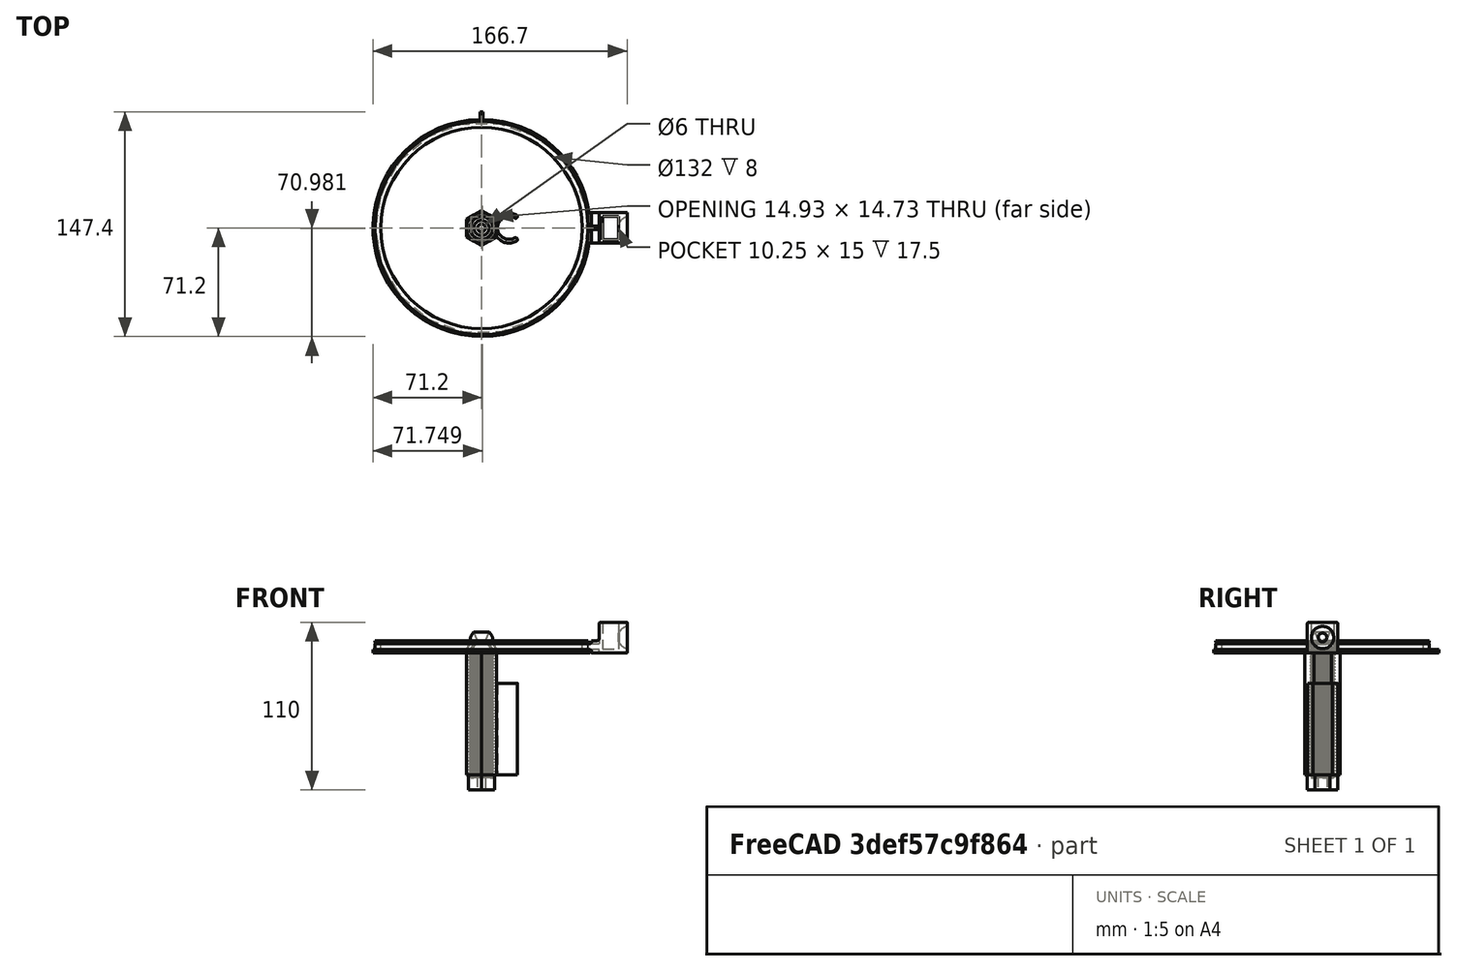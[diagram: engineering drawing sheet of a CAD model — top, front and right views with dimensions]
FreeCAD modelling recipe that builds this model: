
FCSTD DOCUMENT  (FreeCAD 0.17R13519 (Git))
Label: Pop Filter
License: All rights reserved
LicenseURL: http://en.wikipedia.org/wiki/All_rights_reserved
objects: Sketcher::SketchObject×17, PartDesign::Pad×8, PartDesign::Body×5, App::Part×5, PartDesign::Pocket×5, PartDesign::Revolution×4, PartDesign::Plane×2, PartDesign::Fillet×2, Part::FeaturePython×2, PartDesign::Line×1, PartDesign::Groove×1, PartDesign::Chamfer×1, PartDesign::Boolean×1, PartDesign::FeatureBase×1
note: 68 computed .brp shape members not serialized (recipe doc carries the construction recipe); baked Part::Feature solids carry a one-line shape summary decoded from their .brp

FEATURE [Sketcher::SketchObject] Sketch001  label="Sketch"
  MapMode = 5
  Placement = pos=(0,0,0) rot=(1,0,0;1.5708rad)
  Support = -> [XZ_Plane]
  sketch-geometry (6):
    g0: ArcOfCircle CenterX=0 CenterY=8 CenterZ=0 NormalX=0 NormalY=0 NormalZ=1 AngleXU=0 Radius=7.5 StartAngle=6.03051 EndAngle=7.12425
    g1: ArcOfCircle CenterX=0 CenterY=0 CenterZ=0 NormalX=0 NormalY=0 NormalZ=1 AngleXU=0 Radius=7.5 StartAngle=0 EndAngle=0.841069
    g2: ArcOfCircle CenterX=0 CenterY=0 CenterZ=0 NormalX=0 NormalY=0 NormalZ=1 AngleXU=0 Radius=9.5 StartAngle=0 EndAngle=0.700679
    g3: LineSegment StartX=5 StartY=5.59017 StartZ=0 EndX=2.5 EndY=8 EndZ=0
    g4: LineSegment StartX=7.5 StartY=0 StartZ=0 EndX=9.5 EndY=0 EndZ=0
    g5: LineSegment StartX=2.5 StartY=8 StartZ=0 EndX=5 EndY=13.5902 EndZ=0
  constraints (19):
    c: PointOnObject(g0,g-2)
    c: Radius(g0) = 7.5
    c: Coincident(g1,g-1)
    c: DistanceY(g-1,g1) = 0
    c: DistanceX(g-1,g1) = 5
    c: Radius(g1) = 7.5
    c: Coincident(g2,g-1)
    c: Coincident(g2,g0)
    c: PointOnObject(g2,g-1)
    c: DistanceX(g1,g2) = 2
    c: Coincident(g3,g1)
    c: Coincident(g4,g1)
    c: Coincident(g4,g2)
    c: DistanceY(g0,g3) = 0
    c: DistanceX(g0,g3) = 2.5
    c: Coincident(g5,g3)
    c: Coincident(g5,g0)
    c: DistanceX(g0,g0) = 5
    c: DistanceY(g-1,g0) = 8
FEATURE [PartDesign::Revolution] Revolution
  Angle = 360
  Axis = (0,0,1)
  Base = (0,0,0)
  Placement = pos=(0,0,0) rot=(1,0,0;1.5708rad)
  Profile = -> Sketch001
  ReferenceAxis = -> Sketch001 [V_Axis]
  Reversed = true
FEATURE [PartDesign::Body] Body  label="Arm Section Body"
  Group = -> [Sketch001,Revolution]
  Origin = -> Origin
  Tip = -> Revolution
FEATURE [App::Part] Part  label="Arm Section"
  Group = -> [Body]
  License = CC BY 3.0
  LicenseURL = http://creativecommons.org/licenses/by/3.0/
  Origin = -> Origin001
FEATURE [Sketcher::SketchObject] Sketch002  label="Sketch001"
  MapMode = 5
  Placement = pos=(0,0,0) rot=(1,0,0;1.5708rad)
  Support = -> [XZ_Plane002]
  sketch-geometry (8):
    g0: LineSegment StartX=70 StartY=1 StartZ=0 EndX=70 EndY=0 EndZ=0
    g1: ArcOfCircle CenterX=70 CenterY=1.5 CenterZ=0 NormalX=0 NormalY=0 NormalZ=1 AngleXU=0 Radius=0.5 StartAngle=1.5708 EndAngle=4.71239
    g2: LineSegment StartX=70 StartY=8 StartZ=0 EndX=70 EndY=7 EndZ=0
    g3: ArcOfCircle CenterX=70 CenterY=6.5 CenterZ=0 NormalX=0 NormalY=0 NormalZ=1 AngleXU=0 Radius=0.5 StartAngle=1.5708 EndAngle=4.71239
    g4: LineSegment StartX=70 StartY=2 StartZ=0 EndX=70 EndY=6 EndZ=0
    g5: LineSegment StartX=70 StartY=0 StartZ=0 EndX=66 EndY=0 EndZ=0
    g6: LineSegment StartX=66 StartY=0 StartZ=0 EndX=66 EndY=8 EndZ=0
    g7: LineSegment StartX=66 StartY=8 StartZ=0 EndX=70 EndY=8 EndZ=0
  constraints (27):
    c: Vertical(g0)
    c: PointOnObject(g0,g-1)
    c: DistanceX(g-1,g0) = 70  '70'
    c: Coincident(g1,g0)
    c: DistanceX(g0,g1) = 0
    c: DistanceY(g0,g0) = 1
    c: Radius(g1) = 0.5
    c: Vertical(g2)
    c: DistanceY(g2,g2) = 1
    c: Coincident(g3,g2)
    c: Radius(g3) = 0.5
    c: DistanceX(g2,g3) = 0
    c: Coincident(g4,g1)
    c: Coincident(g4,g3)
    c: Vertical(g4)
    c: DistanceX(g3,g2) = 0
    c: DistanceX(g1,g0) = 0
    c: DistanceY(g0,g2) = 8
    c: Coincident(g6,g5)
    c: Vertical(g6)
    c: PointOnObject(g7,g6)
    c: Horizontal(g7)
    c: Horizontal(g5)
    c: Coincident(g6,g7)
    c: Coincident(g0,g5)
    c: Coincident(g7,g2)
    c: DistanceX(g7,g7) = 4
FEATURE [PartDesign::Revolution] Revolution001
  Angle = 360
  Axis = (0,0,1)
  Base = (0,0,0)
  Placement = pos=(0,0,0) rot=(1,0,0;1.5708rad)
  Profile = -> Sketch002
  ReferenceAxis = -> Sketch002 [V_Axis]
  Reversed = true
FEATURE [PartDesign::Plane] DatumPlane
  MapMode = 49
  Placement = pos=(70,-1e-12,6) rot=(0,1,0;1.5708rad)
  Support = -> [Revolution001]
FEATURE [Sketcher::SketchObject] Sketch  label="Sketch002"
  ExternalGeometry = -> [Revolution001]
  MapMode = 5
  Placement = pos=(70,-1e-12,6) rot=(0,1,0;1.5708rad)
  Support = -> [DatumPlane]
  sketch-geometry (4):
    g0: LineSegment StartX=0 StartY=10 StartZ=0 EndX=4 EndY=10 EndZ=0
    g1: LineSegment StartX=4 StartY=10 StartZ=0 EndX=4 EndY=-10 EndZ=0
    g2: LineSegment StartX=4 StartY=-10 StartZ=0 EndX=0 EndY=-10 EndZ=0
    g3: LineSegment StartX=0 StartY=-10 StartZ=0 EndX=0 EndY=10 EndZ=0
  constraints (11):
    c: Coincident(g1,g2)
    c: Coincident(g2,g3)
    c: Coincident(g3,g0)
    c: Horizontal(g0)
    c: Horizontal(g2)
    c: Vertical(g1)
    c: Vertical(g3)
    c: DistanceY(g1,g1) = 20  '7.5*2+2.5*2'
    c: Coincident(g1,g0)
    c: Symmetric(g0,g1,g-3)
    c: Symmetric(g0,g2,g-1)
FEATURE [PartDesign::Pad] Pad
  BaseFeature = -> Revolution001
  Length = 2
  Length2 = 2
  Placement = pos=(0,0,0) rot=(1,0,0;1.5708rad)
  Profile = -> Sketch
  Type = 4
FEATURE [Sketcher::SketchObject] Sketch003
  ExternalGeometry = -> [Pad]
  MapMode = 5
  Placement = pos=(72,0,0) rot=(0.707107,0,0.707107;3.14159rad)
  Support = -> [Pad]
  sketch-geometry (4):
    g0: LineSegment StartX=0 StartY=10 StartZ=0 EndX=8 EndY=10 EndZ=0
    g1: LineSegment StartX=8 StartY=10 StartZ=0 EndX=8 EndY=-10 EndZ=0
    g2: LineSegment StartX=8 StartY=-10 StartZ=0 EndX=0 EndY=-10 EndZ=0
    g3: LineSegment StartX=0 StartY=-10 StartZ=0 EndX=0 EndY=10 EndZ=0
  constraints (12):
    c: Coincident(g0,g1)
    c: Coincident(g1,g2)
    c: Coincident(g2,g3)
    c: Coincident(g3,g0)
    c: Horizontal(g0)
    c: Horizontal(g2)
    c: Vertical(g1)
    c: Vertical(g3)
    c: PointOnObject(g-6,g0)
    c: PointOnObject(g-4,g2)
    c: PointOnObject(g-1,g3)
    c: PointOnObject(g-7,g1)
FEATURE [PartDesign::Pad] Pad001
  BaseFeature = -> Pad
  Length = 5
  Length2 = 100
  Placement = pos=(0,0,0) rot=(1,0,0;1.5708rad)
  Profile = -> Sketch003
  Type = 0
FEATURE [Sketcher::SketchObject] Sketch004
  ExternalGeometry = -> [Pad001]
  MapMode = 5
  Placement = pos=(0,0,0) rot=(1,0,0;3.14159rad)
  Support = -> [Pad001]
  sketch-geometry (4):
    g0: LineSegment StartX=72 StartY=1.1 StartZ=0 EndX=77 EndY=1.1 EndZ=0
    g1: LineSegment StartX=77 StartY=1.1 StartZ=0 EndX=77 EndY=-1.1 EndZ=0
    g2: LineSegment StartX=77 StartY=-1.1 StartZ=0 EndX=72 EndY=-1.1 EndZ=0
    g3: LineSegment StartX=72 StartY=-1.1 StartZ=0 EndX=72 EndY=1.1 EndZ=0
  constraints (12):
    c: Coincident(g0,g1)
    c: Coincident(g1,g2)
    c: Coincident(g2,g3)
    c: Coincident(g3,g0)
    c: Horizontal(g0)
    c: Horizontal(g2)
    c: Vertical(g1)
    c: Vertical(g3)
    c: PointOnObject(g0,g-3)
    c: PointOnObject(g0,g-4)
    c: Symmetric(g0,g2,g-1)
    c: DistanceY(g1,g0) = 2.2
FEATURE [PartDesign::Pocket] Pocket
  BaseFeature = -> Pad001
  Length = 2
  Length2 = 100
  Placement = pos=(0,0,0) rot=(1,0,0;1.5708rad)
  Profile = -> Sketch004
  Type = 0
FEATURE [Sketcher::SketchObject] Sketch005
  ExternalGeometry = -> [Pocket]
  MapMode = 5
  Placement = pos=(0,-1e-12,8) rot=(0,0,1;3.14159rad)
  Support = -> [Pocket]
  sketch-geometry (4):
    g0: LineSegment StartX=-77 StartY=1.1 StartZ=0 EndX=-72 EndY=1.1 EndZ=0
    g1: LineSegment StartX=-72 StartY=1.1 StartZ=0 EndX=-72 EndY=-1.1 EndZ=0
    g2: LineSegment StartX=-72 StartY=-1.1 StartZ=0 EndX=-77 EndY=-1.1 EndZ=0
    g3: LineSegment StartX=-77 StartY=-1.1 StartZ=0 EndX=-77 EndY=1.1 EndZ=0
  constraints (12):
    c: Coincident(g0,g1)
    c: Coincident(g1,g2)
    c: Coincident(g2,g3)
    c: Coincident(g3,g0)
    c: Horizontal(g0)
    c: Horizontal(g2)
    c: Vertical(g1)
    c: Vertical(g3)
    c: PointOnObject(g0,g-3)
    c: Symmetric(g0,g1,g-1)
    c: DistanceY(g2,g0) = 2.2
    c: PointOnObject(g0,g-4)
FEATURE [PartDesign::Pocket] Pocket001
  BaseFeature = -> Pocket
  Length = 2
  Length2 = 100
  Placement = pos=(0,0,0) rot=(1,0,0;1.5708rad)
  Profile = -> Sketch005
  Type = 0
FEATURE [Sketcher::SketchObject] Sketch006
  ExternalGeometry = -> [Pocket001]
  MapMode = 5
  Placement = pos=(77,0,0) rot=(0.707107,0,0.707107;3.14159rad)
  Support = -> [Pocket001]
  sketch-geometry (4):
    g0: LineSegment StartX=0 StartY=10 StartZ=0 EndX=20 EndY=10 EndZ=0
    g1: LineSegment StartX=20 StartY=10 StartZ=0 EndX=20 EndY=-10 EndZ=0
    g2: LineSegment StartX=20 StartY=-10 StartZ=0 EndX=0 EndY=-10 EndZ=0
    g3: LineSegment StartX=0 StartY=-10 StartZ=0 EndX=0 EndY=10 EndZ=0
  constraints (12):
    c: Coincident(g0,g1)
    c: Coincident(g1,g2)
    c: Coincident(g2,g3)
    c: Coincident(g3,g0)
    c: Horizontal(g0)
    c: Horizontal(g2)
    c: Vertical(g1)
    c: Vertical(g3)
    c: PointOnObject(g-3,g0)
    c: Symmetric(g0,g1,g-1)
    c: PointOnObject(g-1,g3)
    c: DistanceX(g0,g0) = 20  '7.5*2+2.5*2'
FEATURE [PartDesign::Pad] Pad002
  BaseFeature = -> Pocket001
  Length = 18.5
  Length2 = 100
  Placement = pos=(0,0,0) rot=(1,0,0;1.5708rad)
  Profile = -> Sketch006
  Type = 0
FEATURE [Sketcher::SketchObject] Sketch007
  AttachmentOffset = pos=(0,0,1.5) rot=(0,0,1;0rad)
  ExternalGeometry = -> [Pad002]
  MapMode = 5
  Placement = pos=(97,0,0) rot=(0.707107,0,0.707107;3.14159rad)
  Support = -> [Pad002]
  sketch-geometry (2):
    g0: ArcOfCircle CenterX=10 CenterY=0 CenterZ=0 NormalX=0 NormalY=0 NormalZ=1 AngleXU=0 Radius=7.5 StartAngle=3.14159 EndAngle=6.28319
    g1: LineSegment StartX=17.5 StartY=0 StartZ=0 EndX=2.5 EndY=0 EndZ=0
  constraints (7):
    c: PointOnObject(g0,g-1)
    c: PointOnObject(g0,g-1)
    c: PointOnObject(g0,g-1)
    c: Radius(g0) = 7.5
    c: DistanceX(g0,g-3) = 2.5
    c: Coincident(g1,g0)
    c: Coincident(g1,g0)
FEATURE [PartDesign::Line] DatumLine
  AttacherType = Attacher::AttachEngineLine
  MapMode = 29
  Placement = pos=(97,0,0) rot=(0,1,0;3.14159rad)
  Support = -> [Sketch007]
FEATURE [PartDesign::Groove] Groove
  Angle = 360
  Axis = (0,0,-1)
  Base = (97,0,0)
  BaseFeature = -> Pad002
  Placement = pos=(0,0,0) rot=(1,0,0;1.5708rad)
  Profile = -> Sketch007
  ReferenceAxis = -> DatumLine
FEATURE [Sketcher::SketchObject] Sketch008
  ExternalGeometry = -> [Groove]
  MapMode = 5
  Placement = pos=(0,-2e-12,20) rot=(0,0,1;3.14159rad)
  Support = -> [Groove]
  sketch-geometry (4):
    g0: LineSegment StartX=-89.75 StartY=7.5 StartZ=0 EndX=-79.5 EndY=7.5 EndZ=0
    g1: LineSegment StartX=-79.5 StartY=7.5 StartZ=0 EndX=-79.5 EndY=-7.5 EndZ=0
    g2: LineSegment StartX=-79.5 StartY=-7.5 StartZ=0 EndX=-89.75 EndY=-7.5 EndZ=0
    g3: LineSegment StartX=-89.75 StartY=-7.5 StartZ=0 EndX=-89.75 EndY=7.5 EndZ=0
  constraints (12):
    c: Coincident(g0,g1)
    c: Coincident(g1,g2)
    c: Coincident(g2,g3)
    c: Coincident(g3,g0)
    c: Horizontal(g0)
    c: Horizontal(g2)
    c: Vertical(g1)
    c: Vertical(g3)
    c: DistanceY(g-3,g2) = 2.5
    c: DistanceY(g0,g-3) = 2.5
    c: DistanceX(g-3,g0) = 5.75
    c: DistanceX(g0,g-4) = 2.5
FEATURE [PartDesign::Pocket] Pocket002
  BaseFeature = -> Groove
  Length = 17.5
  Length2 = 100
  Placement = pos=(0,0,0) rot=(1,0,0;1.5708rad)
  Profile = -> Sketch008
  Type = 0
FEATURE [PartDesign::Fillet] Fillet
  Base = -> Pocket002 [Edge37,Edge38,Edge64,Edge75,Edge13,Edge10]
  BaseFeature = -> Pocket002
  Placement = pos=(0,0,0) rot=(1,0,0;1.5708rad)
  Radius = 1
FEATURE [PartDesign::Chamfer] Chamfer
  Base = -> Fillet [Edge118]
  BaseFeature = -> Fillet
  Placement = pos=(0,0,0) rot=(1,0,0;1.5708rad)
  Size = 1
FEATURE [PartDesign::Fillet] Fillet001
  Base = -> Chamfer [Face25,Face34,Edge18,Edge36,Edge24,Edge15,Edge16,Edge41,Edge50]
  BaseFeature = -> Chamfer
  Placement = pos=(0,0,0) rot=(1,0,0;1.5708rad)
  Radius = 1
FEATURE [PartDesign::Body] Body001  label="Pop Filter Body"
  Group = -> [Sketch002,Revolution001,DatumPlane,Sketch,Pad,Sketch003,Pad001,Sketch004,Pocket,Sketch005,Pocket001,Sketch006,Pad002,Sketch007,DatumLine,Groove,Sketch008,Pocket002,Fillet,Chamfer,Fillet001]
  Origin = -> Origin002
  Tip = -> Fillet001
FEATURE [App::Part] Part001  label="Pop Filter"
  Group = -> [Body001]
  License = CC BY 3.0
  LicenseURL = http://creativecommons.org/licenses/by/3.0/
  Origin = -> Origin003
FEATURE [Sketcher::SketchObject] Sketch009
  MapMode = 5
  Placement = pos=(0,0,0) rot=(0.57735,0.57735,0.57735;2.0944rad)
  Support = -> [YZ_Plane004]
  sketch-geometry (5):
    g0: LineSegment StartX=70.2 StartY=1 StartZ=0 EndX=70.2 EndY=0 EndZ=0
    g1: ArcOfCircle CenterX=70.2 CenterY=1.5 CenterZ=0 NormalX=0 NormalY=0 NormalZ=1 AngleXU=0 Radius=0.5 StartAngle=1.5708 EndAngle=4.71239
    g2: LineSegment StartX=70.2 StartY=0 StartZ=0 EndX=71.2 EndY=0 EndZ=0
    g3: LineSegment StartX=70.2 StartY=2 StartZ=0 EndX=71.2 EndY=2 EndZ=0
    g4: LineSegment StartX=71.2 StartY=2 StartZ=0 EndX=71.2 EndY=0 EndZ=0
  constraints (16):
    c: Vertical(g0)
    c: PointOnObject(g0,g-1)
    c: DistanceX(g-1,g0) = 70.2  '70.2'
    c: Coincident(g1,g0)
    c: DistanceX(g0,g1) = 0
    c: DistanceY(g0,g0) = 1
    c: Radius(g1) = 0.5
    c: DistanceX(g1,g0) = 0
    c: Coincident(g2,g0)
    c: PointOnObject(g2,g-1)
    c: Coincident(g3,g1)
    c: Horizontal(g3)
    c: Coincident(g4,g3)
    c: Coincident(g4,g2)
    c: Vertical(g4)
    c: DistanceX(g2,g2) = 1
FEATURE [PartDesign::Revolution] Revolution002
  Angle = 360
  Axis = (0,0,1)
  Base = (0,0,0)
  Placement = pos=(0,0,0) rot=(0.57735,0.57735,0.57735;2.0944rad)
  Profile = -> Sketch009
  ReferenceAxis = -> Sketch009 [V_Axis]
  Reversed = true
FEATURE [PartDesign::Plane] DatumPlane001
  MapMode = 52
  Placement = pos=(0,71.2,2) rot=(-1,0,0;1.5708rad)
  Support = -> [Revolution002]
FEATURE [Sketcher::SketchObject] Sketch010
  ExternalGeometry = -> [Revolution002]
  MapMode = 5
  Placement = pos=(0,71.2,2) rot=(-1,0,0;1.5708rad)
  Support = -> [DatumPlane001]
  sketch-geometry (4):
    g0: LineSegment StartX=-1.1 StartY=2 StartZ=0 EndX=1.1 EndY=2 EndZ=0
    g1: LineSegment StartX=1.1 StartY=2 StartZ=0 EndX=1.1 EndY=0 EndZ=0
    g2: LineSegment StartX=1.1 StartY=0 StartZ=0 EndX=-1.1 EndY=0 EndZ=0
    g3: LineSegment StartX=-1.1 StartY=0 StartZ=0 EndX=-1.1 EndY=2 EndZ=0
  constraints (11):
    c: Coincident(g0,g1)
    c: Coincident(g1,g2)
    c: Coincident(g2,g3)
    c: Coincident(g3,g0)
    c: Horizontal(g0)
    c: Horizontal(g2)
    c: Vertical(g1)
    c: Vertical(g3)
    c: Symmetric(g1,g2,g-1)
    c: PointOnObject(g-3,g0)
    c: DistanceX(g0,g0) = 2.2
FEATURE [PartDesign::Pad] Pad003
  BaseFeature = -> Revolution002
  Length = 5
  Length2 = 1
  Placement = pos=(0,0,0) rot=(0.57735,0.57735,0.57735;2.0944rad)
  Profile = -> Sketch010
  Type = 4
FEATURE [Sketcher::SketchObject] Sketch011
  ExternalGeometry = -> [Pad003]
  MapMode = 5
  Placement = pos=(0,0,2) rot=(0,0,-1;1.5708rad)
  Support = -> [Pad003]
  sketch-geometry (4):
    g0: LineSegment StartX=-76.2 StartY=0.1 StartZ=0 EndX=0 EndY=0.1 EndZ=0
    g1: LineSegment StartX=0 StartY=0.1 StartZ=0 EndX=0 EndY=-0.1 EndZ=0
    g2: LineSegment StartX=0 StartY=-0.1 StartZ=0 EndX=-76.2 EndY=-0.1 EndZ=0
    g3: LineSegment StartX=-76.2 StartY=-0.1 StartZ=0 EndX=-76.2 EndY=0.1 EndZ=0
  constraints (12):
    c: Coincident(g0,g1)
    c: Coincident(g1,g2)
    c: Coincident(g2,g3)
    c: Coincident(g3,g0)
    c: Horizontal(g0)
    c: Horizontal(g2)
    c: Vertical(g1)
    c: Vertical(g3)
    c: Symmetric(g1,g0,g-1)
    c: DistanceY(g1,g0) = 0.2
    c: PointOnObject(g2,g-3)
    c: PointOnObject(g1,g-2)
FEATURE [PartDesign::Pocket] Pocket003
  BaseFeature = -> Pad003
  Length = 2
  Length2 = 100
  Placement = pos=(0,0,0) rot=(0.57735,0.57735,0.57735;2.0944rad)
  Profile = -> Sketch011
  Type = 0
FEATURE [Sketcher::SketchObject] Sketch012
  MapMode = 5
  Placement = pos=(0,0,0) rot=(1,0,0;1.5708rad)
  Support = -> [XZ_Plane006]
  sketch-geometry (5):
    g0: ArcOfCircle CenterX=0 CenterY=8 CenterZ=0 NormalX=0 NormalY=0 NormalZ=1 AngleXU=0 Radius=7.5 StartAngle=6.11362 EndAngle=7.12425
    g1: ArcOfCircle CenterX=0 CenterY=0 CenterZ=0 NormalX=0 NormalY=0 NormalZ=1 AngleXU=0 Radius=10 StartAngle=0 EndAngle=0.738849
    g2: LineSegment StartX=8 StartY=0 StartZ=0 EndX=10 EndY=0 EndZ=0
    g3: LineSegment StartX=2.5 StartY=8 StartZ=0 EndX=5 EndY=13.5902 EndZ=0
    g4: LineSegment StartX=2.5 StartY=8 StartZ=0 EndX=8 EndY=0 EndZ=0
  constraints (16):
    c: PointOnObject(g0,g-2)
    c: Radius(g0) = 7.5
    c: DistanceY(g-1,g2) = 0
    c: Coincident(g1,g-1)
    c: Coincident(g1,g0)
    c: PointOnObject(g1,g-1)
    c: Coincident(g2,g1)
    c: DistanceY(g0,g3) = 0
    c: DistanceX(g0,g3) = 2.5
    c: Coincident(g3,g0)
    c: DistanceX(g0,g0) = 5
    c: DistanceY(g-1,g0) = 8
    c: DistanceX(g-1,g1) = 10
    c: Coincident(g4,g2)
    c: Coincident(g4,g3)
    c: DistanceX(g-1,g2) = 8
FEATURE [PartDesign::Revolution] Revolution003
  Angle = 360
  Axis = (0,0,1)
  Base = (0,0,0)
  Placement = pos=(0,0,0) rot=(1,0,0;1.5708rad)
  Profile = -> Sketch012
  ReferenceAxis = -> Sketch012 [V_Axis]
  Reversed = true
FEATURE [PartDesign::Pad] Pad004
  BaseFeature = -> Pocket003
  Length = 10
  Length2 = 100
  Placement = pos=(0,0,0) rot=(0.57735,0.57735,0.57735;2.0944rad)
  Profile = -> Revolution003 [Face4]
  Type = 0
FEATURE [PartDesign::Body] Body002  label="Pop Filter Ring Body"
  Group = -> [Sketch009,Revolution002,DatumPlane001,Sketch010,Pad003,Sketch011,Pocket003,Pad004]
  Origin = -> Origin005
  Tip = -> Pad004
FEATURE [App::Part] Part002  label="Pop Filter Ring"
  Group = -> [Body002]
  License = CC BY 3.0
  LicenseURL = http://creativecommons.org/licenses/by/3.0/
  Origin = -> Origin004
FEATURE [Sketcher::SketchObject] Sketch013
  ExternalGeometry = -> [Revolution003]
  MapMode = 5
  Placement = pos=(0,0,0) rot=(1,0,0;3.14159rad)
  Support = -> [Revolution003]
  sketch-geometry (7):
    g0: LineSegment StartX=10 StartY=-5.7735 StartZ=0 EndX=10 EndY=5.7735 EndZ=0
    g1: LineSegment StartX=10 StartY=5.7735 StartZ=0 EndX=0 EndY=11.547 EndZ=0
    g2: LineSegment StartX=0 StartY=11.547 StartZ=0 EndX=-10 EndY=5.7735 EndZ=0
    g3: LineSegment StartX=-10 StartY=5.7735 StartZ=0 EndX=-10 EndY=-5.7735 EndZ=0
    g4: LineSegment StartX=-10 StartY=-5.7735 StartZ=0 EndX=0 EndY=-11.547 EndZ=0
    g5: LineSegment StartX=0 StartY=-11.547 StartZ=0 EndX=10 EndY=-5.7735 EndZ=0
    g6: Circle [constr] CenterX=0 CenterY=0 CenterZ=0 NormalX=0 NormalY=0 NormalZ=1 AngleXU=0 Radius=11.547
  constraints (16):
    c: Coincident(g0,g1)
    c: Coincident(g1,g2)
    c: Coincident(g2,g3)
    c: Coincident(g3,g4)
    c: Coincident(g4,g5)
    c: Coincident(g5,g0)
    c: Equal(g0, g1-g5) x5
    c: PointOnObject(g0,g6)
    c: PointOnObject(g1,g6)
    c: PointOnObject(g2,g6)
    c: PointOnObject(g3,g6)
    c: PointOnObject(g4,g6)
    c: PointOnObject(g5,g6)
    c: Vertical(g0)
    c: Coincident(g6,g-1)
    c: Tangent(g-3,g0)
FEATURE [PartDesign::Pad] Pad005
  BaseFeature = -> Revolution003
  Length = 80
  Length2 = 100
  Placement = pos=(0,0,0) rot=(1,0,0;1.5708rad)
  Profile = -> Sketch013
  Type = 0
FEATURE [Part::FeaturePython] ScrewTap  label="M16x80.0-ScrewTap"  # Fasteners workbench fastener (typed FeaturePython)
  diameter = 13
  invert = false
  length = 80
  matchOuter = false
  offset = 0
  thread = true
FEATURE [PartDesign::Boolean] Boolean
  BaseFeature = -> Pad005
  Group = -> [ScrewTap]
  Type = 1
FEATURE [Sketcher::SketchObject] Sketch014
  ExternalGeometry = -> [Boolean]
  MapMode = 5
  Placement = pos=(0,8e-12,-80) rot=(1,0,0;3.14159rad)
  Support = -> [Boolean]
  sketch-geometry (8):
    g0: ArcOfCircle CenterX=18 CenterY=0 CenterZ=0 NormalX=0 NormalY=0 NormalZ=1 AngleXU=0 Radius=7.5 StartAngle=1.0472 EndAngle=5.23599
    g1: ArcOfCircle CenterX=18 CenterY=0 CenterZ=0 NormalX=0 NormalY=0 NormalZ=1 AngleXU=0 Radius=9.86577 StartAngle=3.76673 EndAngle=5.23599
    g2: ArcOfCircle CenterX=22.3414 CenterY=-7.5196 CenterZ=0 NormalX=0 NormalY=0 NormalZ=1 AngleXU=0 Radius=1.18288 StartAngle=5.23599 EndAngle=8.37758
    g3: ArcOfCircle CenterX=22.3414 CenterY=7.5196 CenterZ=0 NormalX=0 NormalY=0 NormalZ=1 AngleXU=0 Radius=1.18288 StartAngle=4.18879 EndAngle=7.33038
    g4: ArcOfCircle CenterX=18 CenterY=0 CenterZ=0 NormalX=0 NormalY=0 NormalZ=1 AngleXU=0 Radius=9.86577 StartAngle=1.0472 EndAngle=2.51646
    g5: LineSegment StartX=10 StartY=5.7735 StartZ=0 EndX=10 EndY=-5.7735 EndZ=0
    g6: LineSegment [constr] StartX=22.3414 StartY=7.5196 StartZ=0 EndX=10 EndY=0 EndZ=0
    g7: LineSegment [constr] StartX=22.3414 StartY=-7.5196 StartZ=0 EndX=10 EndY=0 EndZ=0
  constraints (20):
    c: Radius(g0) = 7.5  '15/2'
    c: Angle(g0) = 4.18879  '240'
    c: DistanceX(g-3,g0) = 8
    c: DistanceY(g-1,g0) = 0
    c: Coincident(g1,g0)
    c: Coincident(g1,g-3)
    c: Tangent(g2,g0) = 1.5708
    c: Tangent(g2,g1) = -1.5708
    c: Tangent(g3,g0) = 1.5708
    c: Tangent(g4,g3) = -1.5708
    c: Coincident(g4,g0)
    c: Coincident(g5,g4)
    c: Coincident(g5,g1)
    c: Coincident(g6,g3)
    c: PointOnObject(g6,g5)
    c: Coincident(g7,g6)
    c: Coincident(g7,g2)
    c: Symmetric(g1,g4,g6)
    c: Equal(g6,g7)
    c: Coincident(g4,g-4)
FEATURE [PartDesign::Pad] Pad006
  BaseFeature = -> Boolean
  Length = 60
  Length2 = 100
  Profile = -> Sketch014
  Reversed = true
  Type = 0
FEATURE [PartDesign::Body] Body003  label="Arm Back Body"
  Group = -> [Sketch012,Revolution003,Sketch013,Pad005,Boolean,Sketch014,Pad006]
  Origin = -> Origin006
  Tip = -> Pad006
FEATURE [App::Part] Part003  label="Arm Back"
  Group = -> [Body003]
  License = CC BY 3.0
  LicenseURL = http://creativecommons.org/licenses/by/3.0/
  Origin = -> Origin007
FEATURE [Part::FeaturePython] ScrewTap001  label="M16x78.0-ScrewTap"  # Fasteners workbench fastener (typed FeaturePython)
  diameter = 13
  invert = false
  length = 78
  matchOuter = false
  offset = 0
  thread = true
FEATURE [PartDesign::FeatureBase] BaseFeature
  BaseFeature = -> ScrewTap001
FEATURE [Sketcher::SketchObject] Sketch015
  MapMode = 5
  Placement = pos=(0,0,-80) rot=(1,0,0;3.14159rad)
  Support = -> [BaseFeature]
  sketch-geometry (7):
    g0: LineSegment StartX=8.66025 StartY=5 StartZ=0 EndX=9e-12 EndY=10 EndZ=0
    g1: LineSegment StartX=9e-12 StartY=10 StartZ=0 EndX=-8.66025 EndY=5 EndZ=0
    g2: LineSegment StartX=-8.66025 StartY=5 StartZ=0 EndX=-8.66025 EndY=-5 EndZ=0
    g3: LineSegment StartX=-8.66025 StartY=-5 StartZ=0 EndX=1.3e-11 EndY=-10 EndZ=0
    g4: LineSegment StartX=1.3e-11 StartY=-10 StartZ=0 EndX=8.66025 EndY=-5 EndZ=0
    g5: LineSegment StartX=8.66025 StartY=-5 StartZ=0 EndX=8.66025 EndY=5 EndZ=0
    g6: Circle [constr] CenterX=0 CenterY=0 CenterZ=0 NormalX=0 NormalY=0 NormalZ=1 AngleXU=0 Radius=10
  constraints (16):
    c: Coincident(g0,g1)
    c: Coincident(g1,g2)
    c: Coincident(g2,g3)
    c: Coincident(g3,g4)
    c: Coincident(g4,g5)
    c: Coincident(g5,g0)
    c: Equal(g0, g1-g5) x5
    c: PointOnObject(g0,g6)
    c: PointOnObject(g1,g6)
    c: PointOnObject(g2,g6)
    c: PointOnObject(g3,g6)
    c: PointOnObject(g4,g6)
    c: PointOnObject(g5,g6)
    c: Coincident(g6,g-1)
    c: Vertical(g5)
    c: Radius(g6) = 10
FEATURE [PartDesign::Pad] Pad007
  BaseFeature = -> BaseFeature
  Length = 10
  Length2 = 100
  Profile = -> Sketch015
  Type = 0
FEATURE [Sketcher::SketchObject] Sketch016
  MapMode = 5
  Placement = pos=(0,0,-90) rot=(1,0,0;3.14159rad)
  Support = -> [Pad007]
  sketch-geometry (1):
    g0: Circle CenterX=0 CenterY=0 CenterZ=0 NormalX=0 NormalY=0 NormalZ=1 AngleXU=0 Radius=3
  constraints (2):
    c: Coincident(g0,g-1)
    c: Radius(g0) = 3
FEATURE [PartDesign::Pocket] Pocket004
  BaseFeature = -> Pad007
  Length = 90
  Length2 = 100
  Profile = -> Sketch016
  Type = 0
FEATURE [PartDesign::Body] Body004  label="Screw Body"
  BaseFeature = -> ScrewTap001
  Group = -> [BaseFeature,Sketch015,Pad007,Sketch016,Pocket004]
  Origin = -> Origin009
  Tip = -> Pocket004
FEATURE [App::Part] Part004  label="Screw"
  Group = -> [Body004,ScrewTap001]
  License = CC BY 3.0
  LicenseURL = http://creativecommons.org/licenses/by/3.0/
  Origin = -> Origin008
